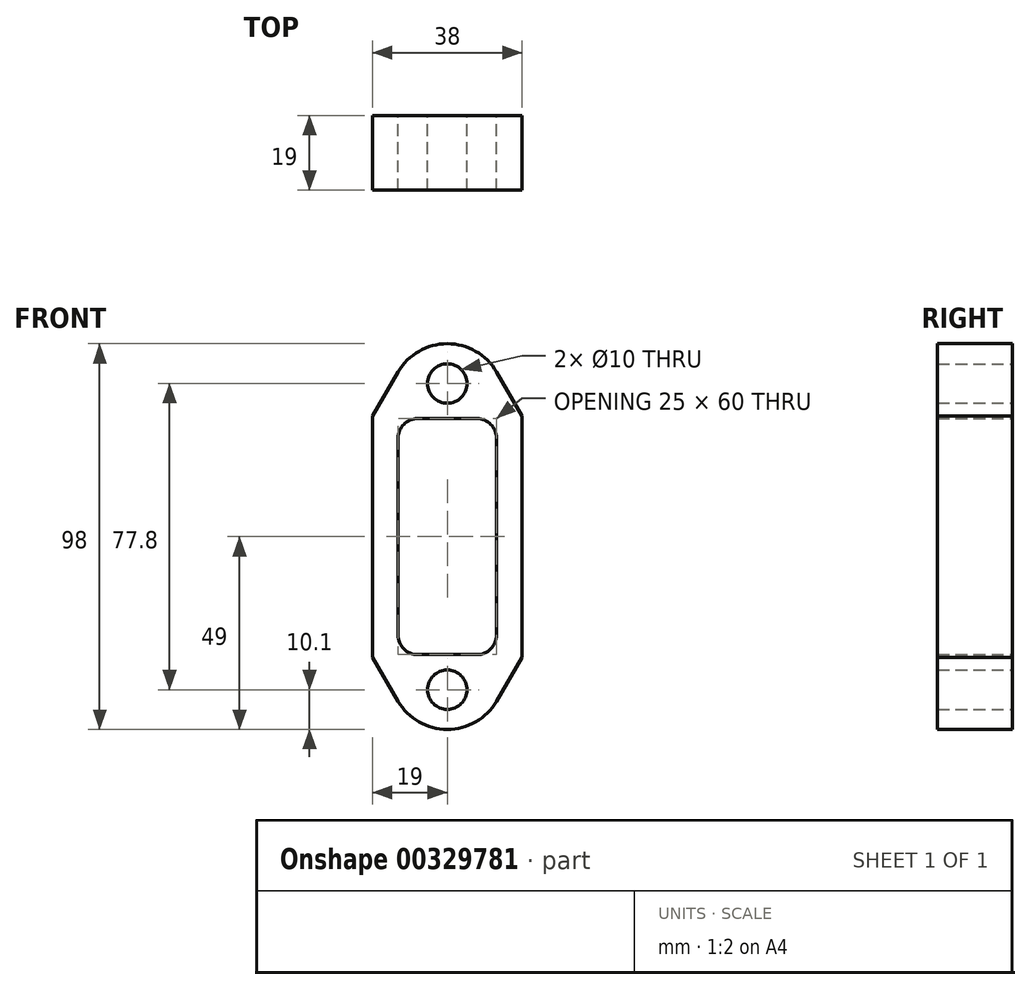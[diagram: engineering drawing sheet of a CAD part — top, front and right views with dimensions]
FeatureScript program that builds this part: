
annotation { "Feature Type Name" : "Feature", "Feature Type Description" : "" }
export const myFeature = defineFeature(function(context is Context, id is Id, definition is map)
    precondition{}
    {
        {
            var Q0;
            Q0=qCreatedBy(makeId("Front.planeOp"),FACE);
            var sketch = newSketch(context, id + "F0", { "sketchPlane" : qUnion([Q0])});
            skLineSegment(sketch, "E0", {"start": v(-19, 30.68) * mm, "end": v(-12.5, 41.82) * mm});
            skPoint(sketch, "E1.endSnap0", {"position": v(-12.5, 0) * mm});
            skLineSegment(sketch, "E2.MirrorCS", {"start": v(19, 30.68) * mm, "end": v(12.5, 41.82) * mm});
            skArc(sketch, "E3", {"start": v(-12.5, 41.82) * mm, "mid": v(0, 49) * mm, "end": v(12.5, 41.82) * mm});
            skCircle(sketch, "E4", {"center": v(0, 38.9) * mm, "radius": 5 * mm});
            skLineSegment(sketch, "E5", {"start": v(-12.5, 0) * mm, "end": v(-12.5, 25) * mm});
            skLineSegment(sketch, "E6", {"start": v(-7.5, 30) * mm, "end": v(0, 30) * mm});
            skLineSegment(sketch, "E7", {"start": v(-19, 30.68) * mm, "end": v(-19, 0) * mm});
            skLineSegment(sketch, "E8.MirrorCS", {"start": v(7.5, 30) * mm, "end": v(0, 30) * mm});
            skLineSegment(sketch, "E9.MirrorCS", {"start": v(12.5, 0) * mm, "end": v(12.5, 25) * mm});
            skLineSegment(sketch, "E10", {"start": v(19, 30.68) * mm, "end": v(19, 0) * mm});
            skLineSegment(sketch, "E11.MirrorCS", {"start": v(-12.5, 0) * mm, "end": v(-12.5, -25) * mm});
            skLineSegment(sketch, "E12.MirrorCS", {"start": v(-19, -30.68) * mm, "end": v(-19, 0) * mm});
            skLineSegment(sketch, "E13.MirrorCS", {"start": v(-19, -30.68) * mm, "end": v(-12.5, -41.82) * mm});
            skArc(sketch, "E14.MirrorCS", {"start": v(-12.5, -41.82) * mm, "mid": v(0, -49) * mm, "end": v(12.5, -41.82) * mm});
            skCircle(sketch, "E15.MirrorC", {"center": v(0, -38.9) * mm, "radius": 5 * mm});
            skLineSegment(sketch, "E16.MirrorCS", {"start": v(7.5, -30) * mm, "end": v(0, -30) * mm});
            skLineSegment(sketch, "E17.MirrorCS", {"start": v(-7.5, -30) * mm, "end": v(0, -30) * mm});
            skLineSegment(sketch, "E18.MirrorCS", {"start": v(19, -30.68) * mm, "end": v(12.5, -41.82) * mm});
            skLineSegment(sketch, "E19.MirrorCS", {"start": v(19, -30.68) * mm, "end": v(19, 0) * mm});
            skLineSegment(sketch, "E20.MirrorCS", {"start": v(12.5, 0) * mm, "end": v(12.5, -25) * mm});
            skPoint(sketch, "E21.visualSharp", {"position": v(-12.5, 30) * mm});
            skArc(sketch, "E21.filletArc", {"start": v(-7.5, 30) * mm, "mid": v(-11.04, 28.54) * mm, "end": v(-12.5, 25) * mm});
            skPoint(sketch, "E22.visualSharp", {"position": v(12.5, 30) * mm});
            skArc(sketch, "E22.filletArc", {"start": v(12.5, 25) * mm, "mid": v(11.04, 28.54) * mm, "end": v(7.5, 30) * mm});
            skPoint(sketch, "E23.visualSharp", {"position": v(-12.5, -30) * mm});
            skArc(sketch, "E23.filletArc", {"start": v(-12.5, -25) * mm, "mid": v(-11.04, -28.54) * mm, "end": v(-7.5, -30) * mm});
            skPoint(sketch, "E24.visualSharp", {"position": v(12.5, -30) * mm});
            skArc(sketch, "E24.filletArc", {"start": v(7.5, -30) * mm, "mid": v(11.04, -28.54) * mm, "end": v(12.5, -25) * mm});
            skSolve(sketch);
        }
        {
            var Q0;
            {var subQ3=sQuery(id+"F0.wireOp",EDGE,"E0");Q0=makeQuery(id+"F0.imprint","IMPRINT",FACE,{"disambiguationData":[TD([[makeQuery(id+"F0.imprint","IMPRINT",EDGE,{"derivedFrom":subQ3}),-1.0]])]});}
            extrude(context, id + "F1", {"entities" : qUnion([Q0]), "depth" : 19 * mm});
        }
    });
